# Revit family: PRD_FrankeWS_SntryTwlDspslBins_RODANSanitaryTowelAndDisposalBin_RODX611
name_source: partatom
category: Furniture
revit_build: Autodesk Revit 2018 (Build: 20190510_1515(x64)
units: mm (PartAtom-declared; Revit-internal decimal feet)

## family parameters
Cut with Voids When Loaded = No
Host = Face
OmniClass Number = 23.40.20.31.11
OmniClass Title = Bins
Room Calculation Point = No
Shared = No

## types (1)
- RODX611
    AssetType = Fixed
    BIMObjectName = PRD_AR_SanitaryTowelDisposalBins_RODANSanitaryTowelAndDisposalBin_RODX611
    Category = Pr_40_50_07_76, Sanitary towel disposal bins
    Color = Stainless steel
    Default Elevation = 500 mm  [stored 1.64042 ft]
    Description = Sanitary towel and disposal bin for wall mounting, stainless steel, surface satin finished, material thickness 0.8 mm, folded front cover, approx. 3.7 liter capacity, removable plastic container inside, incl. stainless steel screws and dowels.
    DurationUnit = year
    Features = stainless steel, 0.80 mm, satin finished, wall mounting, 200x295x165 mm (WxHxD)
    FillingVolume = 3.70 L
    Finish = Satin finished
    FinishAndColour = Stainless steel, satin finished
    Form = Wall mounted
    GrossWeight = 2.61 kg
    IfcExportAs = IfcFurnitureType
    IfcExportType = NOTDEFINED
    IntegralAccessories = includes mounting materials
    MainColor = Stainless steel
    Manufacturer = KWC Group AG
    ManufacturerName = KWC Group AG
    ManufacturerURL = www.kwc.com
    Material = Stainless steel
    Materials = Stainless steel 1.4301
    Model = RODX611
    ModelNumber = 2000090063
    ModelReference = RODX611
    NBSDescription = Sanitary towel disposal bins
    NBSReference = 45-35-72/350
    Name = RODAN Sanitary towel and disposal bin RODX611
    NetWeight = 2.28 kg
    NominalDepth = 165 mm
    NominalHeight = 295 mm  [stored 0.967848 ft]
    NominalLength = 200 mm  [stored 0.656168 ft]
    NominalWidth = 200 mm  [stored 0.656168 ft]
    ProductInformation = https://pim.kwc.com
    Size = 200x295x165 mm
    Style = Sanitary towel and disposal bin
    URL = www.kwc.com
    Uniclass2015Code = Pr_40_50_07_76
    Uniclass2015Title = Sanitary towel disposal bins
    Uniclass2015Version = Products v1.7
    Version = 1
    WarrantyDurationUnit = year
    WasteBinMaterial = PRD_AR_StainlessSteel_SatinFinished

note: [stored X ft] marks values corroborated as IEEE doubles in the binary element streams (Revit-internal decimal feet)

## geometry (parser evidence)
native form markers: Sweep x2
no freeform markers — native parametric forms only
